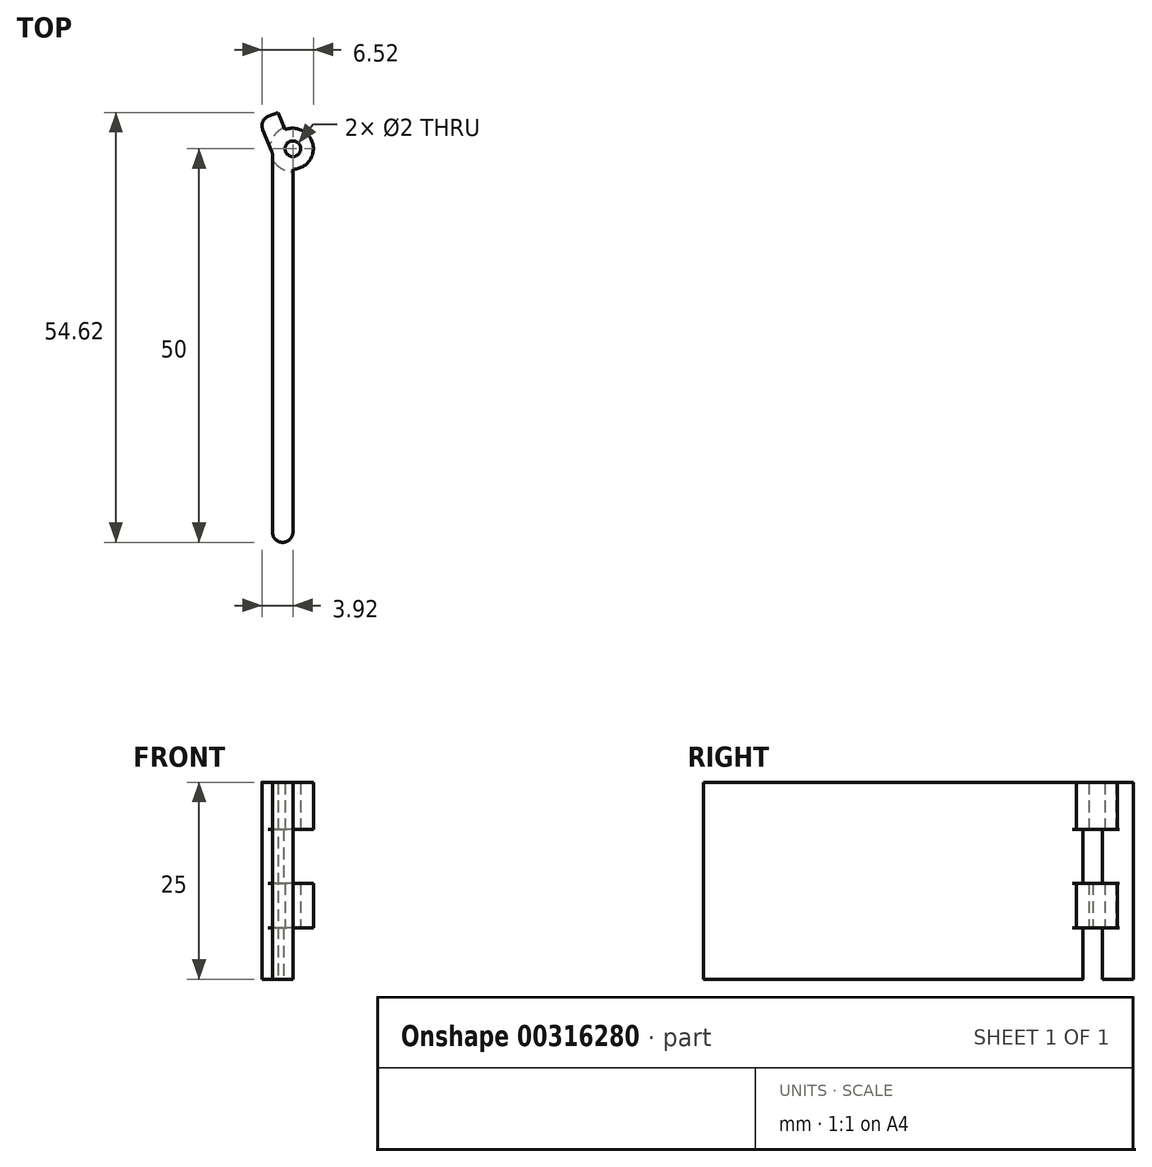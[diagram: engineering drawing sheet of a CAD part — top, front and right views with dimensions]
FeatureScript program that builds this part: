
annotation { "Feature Type Name" : "Feature", "Feature Type Description" : "" }
export const myFeature = defineFeature(function(context is Context, id is Id, definition is map)
    precondition{}
    {
        {
            var Q0;
            Q0=qCreatedBy(makeId("Top.planeOp"),FACE);
            var sketch = newSketch(context, id + "F0", { "sketchPlane" : qUnion([Q0])});
            skLineSegment(sketch, "E0", {"start": v(35.36, -35.36) * mm, "end": v(0, 0) * mm});
            skLineSegment(sketch, "E1", {"start": v(0, 0) * mm, "end": v(0, -50) * mm});
            skCircle(sketch, "E2", {"center": v(0, 0) * mm, "radius": 2.6 * mm});
            skLineSegment(sketch, "E3", {"start": v(0, 0) * mm, "end": v(-1.91, 4.62) * mm});
            skLineSegment(sketch, "E4", {"start": v(0, -50) * mm, "end": v(-2.6, -50) * mm});
            skLineSegment(sketch, "E5", {"start": v(-2.6, -50) * mm, "end": v(-2.6, 0) * mm});
            skCircle(sketch, "E6", {"center": v(0, 0) * mm, "radius": 1 * mm});
            skLineSegment(sketch, "E7", {"start": v(-1.91, 4.62) * mm, "end": v(-4.32, 3.62) * mm});
            skLineSegment(sketch, "E8", {"start": v(-4.32, 3.62) * mm, "end": v(-2.4, -1) * mm});
            skLineSegment(sketch, "E9", {"start": v(-1.91, 4.62) * mm, "end": v(0.49, 5.61) * mm});
            skLineSegment(sketch, "E10", {"start": v(0.49, 5.61) * mm, "end": v(2.4, 1) * mm});
            skLineSegment(sketch, "E11", {"start": v(35.36, -35.36) * mm, "end": v(37.2, -33.52) * mm});
            skLineSegment(sketch, "E12", {"start": v(37.2, -33.52) * mm, "end": v(1.84, 1.84) * mm});
            skSolve(sketch);
        }
        {
            var Q0;
            {var subQ0=sQuery(id+"F0.wireOp",EDGE,"E7");Q0=makeQuery(id+"F0.imprint","IMPRINT",FACE,{"disambiguationData":[TD([[makeQuery(id+"F0.imprint","IMPRINT",EDGE,{"derivedFrom":subQ0}),1.0]])]});}
            var Q1;
            {var subQ0=sQuery(id+"F0.wireOp",EDGE,"E5");var subQ1=sQuery(id+"F0.wireOp",EDGE,"E2");var subQ2=makeQuery(id+"F0.imprint","INTERSECT",VERTEX,{"derivedFrom":[subQ1,subQ0]});Q1=makeQuery(id+"F0.imprint","IMPRINT",FACE,{"disambiguationData":[TD([[makeQuery(id+"F0.imprint","IMPRINT",EDGE,{"disambiguationData":[TD([[subQ2,-1.0]])],"derivedFrom":subQ1}),-1.0]])]});}
            var Q2;
            {var subQ0=sQuery(id+"F0.wireOp",EDGE,"E2");var subQ2=sQuery(id+"F0.wireOp",EDGE,"E1");var subQ3=makeQuery(id+"F0.imprint","INTERSECT",VERTEX,{"derivedFrom":[subQ2,subQ0]});Q2=makeQuery(id+"F0.imprint","IMPRINT",FACE,{"disambiguationData":[TD([[makeQuery(id+"F0.imprint","IMPRINT",EDGE,{"disambiguationData":[TD([[subQ3,1.0]])],"derivedFrom":subQ2}),-1.0]])]});}
            var Q3;
            {var subQ1=sQuery(id+"F0.wireOp",EDGE,"E4");Q3=makeQuery(id+"F0.imprint","IMPRINT",FACE,{"disambiguationData":[TD([[makeQuery(id+"F0.imprint","IMPRINT",EDGE,{"derivedFrom":subQ1}),-1.0]])]});}
            var Q4;
            {var subQ0=sQuery(id+"F0.wireOp",EDGE,"E2");var subQ2=sQuery(id+"F0.wireOp",EDGE,"E0");var subQ3=makeQuery(id+"F0.imprint","INTERSECT",VERTEX,{"derivedFrom":[subQ2,subQ0]});Q4=makeQuery(id+"F0.imprint","IMPRINT",FACE,{"disambiguationData":[TD([[makeQuery(id+"F0.imprint","IMPRINT",EDGE,{"disambiguationData":[TD([[subQ3,-1.0]])],"derivedFrom":subQ2}),-1.0]])]});}
            var Q5;
            {var subQ0=sQuery(id+"F0.wireOp",EDGE,"E2");var subQ1=sQuery(id+"F0.wireOp",EDGE,"E0");var subQ2=makeQuery(id+"F0.imprint","INTERSECT",VERTEX,{"derivedFrom":[subQ1,subQ0]});Q5=makeQuery(id+"F0.imprint","IMPRINT",FACE,{"disambiguationData":[TD([[makeQuery(id+"F0.imprint","IMPRINT",EDGE,{"disambiguationData":[TD([[subQ2,-1.0]])],"derivedFrom":subQ1}),1.0]])]});}
            extrude(context, id + "F1", {"entities" : qUnion([Q0, Q1, Q2, Q3, Q4, Q5]), "depth" : 25 * mm});
        }
        {
            var Q0;
            Q0=makeQuery(id+"F1.opExtrude","CAP_FACE",FACE,{"disambiguationData":[OSD([sQuery(id+"F0.wireOp",EDGE,"E1"),sQuery(id+"F0.wireOp",EDGE,"E2"),sQuery(id+"F0.wireOp",EDGE,"E3"),sQuery(id+"F0.wireOp",EDGE,"E4"),sQuery(id+"F0.wireOp",EDGE,"E5"),sQuery(id+"F0.wireOp",EDGE,"E6"),sQuery(id+"F0.wireOp",EDGE,"E7"),sQuery(id+"F0.wireOp",EDGE,"E8")])],"isStart":false});
            var Q1;
            Q1=makeQuery(id+"F1.opExtrude","CAP_FACE",FACE,{"disambiguationData":[OSD([sQuery(id+"F0.wireOp",EDGE,"E1"),sQuery(id+"F0.wireOp",EDGE,"E2"),sQuery(id+"F0.wireOp",EDGE,"E3"),sQuery(id+"F0.wireOp",EDGE,"E4"),sQuery(id+"F0.wireOp",EDGE,"E5"),sQuery(id+"F0.wireOp",EDGE,"E6"),sQuery(id+"F0.wireOp",EDGE,"E7"),sQuery(id+"F0.wireOp",EDGE,"E8")])],"isStart":true});
            cPlane(context, id + "F2", {"entities" : qUnion([Q0, Q1]), "cplaneType" : CPlaneType.MID_PLANE, "offset" : 25 * mm, "width" : 150 * mm, "height" : 150 * mm});
        }
        {
            var Q0;
            Q0=qCreatedBy(id+"F2.planeOp",FACE);
            var Q1;
            Q1=makeQuery(id+"F1.opExtrude","CAP_FACE",FACE,{"disambiguationData":[OSD([sQuery(id+"F0.wireOp",EDGE,"E1"),sQuery(id+"F0.wireOp",EDGE,"E2"),sQuery(id+"F0.wireOp",EDGE,"E3"),sQuery(id+"F0.wireOp",EDGE,"E4"),sQuery(id+"F0.wireOp",EDGE,"E5"),sQuery(id+"F0.wireOp",EDGE,"E6"),sQuery(id+"F0.wireOp",EDGE,"E7"),sQuery(id+"F0.wireOp",EDGE,"E8")])],"isStart":true});
            cPlane(context, id + "F3", {"entities" : qUnion([Q0, Q1]), "cplaneType" : CPlaneType.MID_PLANE, "offset" : 25 * mm, "width" : 150 * mm, "height" : 150 * mm});
        }
        {
            var Q0;
            Q0=makeQuery(id+"F1.opExtrude","CAP_FACE",FACE,{"disambiguationData":[OSD([sQuery(id+"F0.wireOp",EDGE,"E1"),sQuery(id+"F0.wireOp",EDGE,"E2"),sQuery(id+"F0.wireOp",EDGE,"E3"),sQuery(id+"F0.wireOp",EDGE,"E4"),sQuery(id+"F0.wireOp",EDGE,"E5"),sQuery(id+"F0.wireOp",EDGE,"E6"),sQuery(id+"F0.wireOp",EDGE,"E7"),sQuery(id+"F0.wireOp",EDGE,"E8")])],"isStart":false});
            var Q1;
            Q1=qCreatedBy(id+"F2.planeOp",FACE);
            cPlane(context, id + "F4", {"entities" : qUnion([Q0, Q1]), "cplaneType" : CPlaneType.MID_PLANE, "offset" : 25 * mm, "width" : 150 * mm, "height" : 150 * mm});
        }
        {
            var Q0;
            {var subQ0=sQuery(id+"F0.wireOp",EDGE,"E2");var subQ2=sQuery(id+"F0.wireOp",EDGE,"E1");var subQ3=makeQuery(id+"F0.imprint","INTERSECT",VERTEX,{"derivedFrom":[subQ2,subQ0]});Q0=makeQuery(id+"F0.imprint","IMPRINT",FACE,{"disambiguationData":[TD([[makeQuery(id+"F0.imprint","IMPRINT",EDGE,{"disambiguationData":[TD([[subQ3,1.0]])],"derivedFrom":subQ2}),-1.0]])]});}
            var Q1;
            {var subQ0=sQuery(id+"F0.wireOp",EDGE,"E2");var subQ2=sQuery(id+"F0.wireOp",EDGE,"E0");var subQ3=makeQuery(id+"F0.imprint","INTERSECT",VERTEX,{"derivedFrom":[subQ2,subQ0]});Q1=makeQuery(id+"F0.imprint","IMPRINT",FACE,{"disambiguationData":[TD([[makeQuery(id+"F0.imprint","IMPRINT",EDGE,{"disambiguationData":[TD([[subQ3,-1.0]])],"derivedFrom":subQ2}),-1.0]])]});}
            var Q2;
            {var subQ0=sQuery(id+"F0.wireOp",EDGE,"E2");var subQ1=sQuery(id+"F0.wireOp",EDGE,"E0");var subQ2=makeQuery(id+"F0.imprint","INTERSECT",VERTEX,{"derivedFrom":[subQ1,subQ0]});Q2=makeQuery(id+"F0.imprint","IMPRINT",FACE,{"disambiguationData":[TD([[makeQuery(id+"F0.imprint","IMPRINT",EDGE,{"disambiguationData":[TD([[subQ2,-1.0]])],"derivedFrom":subQ1}),1.0]])]});}
            var Q3;
            Q3=qCreatedBy(id+"F3.planeOp",FACE);
            extrude(context, id + "F5", {"entities" : qUnion([Q0, Q1, Q2]), "endBound" : BoundingType.UP_TO_SURFACE, "endBoundEntityFace" : qUnion([Q3]), "depth" : 25 * mm});
        }
        {
            var Q0;
            {var subQ0=sQuery(id+"F0.wireOp",EDGE,"E2");var subQ2=sQuery(id+"F0.wireOp",EDGE,"E1");var subQ3=makeQuery(id+"F0.imprint","INTERSECT",VERTEX,{"derivedFrom":[subQ2,subQ0]});Q0=makeQuery(id+"F0.imprint","IMPRINT",FACE,{"disambiguationData":[TD([[makeQuery(id+"F0.imprint","IMPRINT",EDGE,{"disambiguationData":[TD([[subQ3,1.0]])],"derivedFrom":subQ2}),-1.0]])]});}
            var Q1;
            {var subQ0=sQuery(id+"F0.wireOp",EDGE,"E2");var subQ1=sQuery(id+"F0.wireOp",EDGE,"E0");var subQ2=makeQuery(id+"F0.imprint","INTERSECT",VERTEX,{"derivedFrom":[subQ1,subQ0]});Q1=makeQuery(id+"F0.imprint","IMPRINT",FACE,{"disambiguationData":[TD([[makeQuery(id+"F0.imprint","IMPRINT",EDGE,{"disambiguationData":[TD([[subQ2,-1.0]])],"derivedFrom":subQ1}),1.0]])]});}
            var Q2;
            {var subQ0=sQuery(id+"F0.wireOp",EDGE,"E2");var subQ2=sQuery(id+"F0.wireOp",EDGE,"E0");var subQ3=makeQuery(id+"F0.imprint","INTERSECT",VERTEX,{"derivedFrom":[subQ2,subQ0]});Q2=makeQuery(id+"F0.imprint","IMPRINT",FACE,{"disambiguationData":[TD([[makeQuery(id+"F0.imprint","IMPRINT",EDGE,{"disambiguationData":[TD([[subQ3,-1.0]])],"derivedFrom":subQ2}),-1.0]])]});}
            var Q3;
            Q3=qCreatedBy(id+"F4.planeOp",FACE);
            var Q4;
            Q4=qCreatedBy(id+"F2.planeOp",FACE);
            extrude(context, id + "F6", {"entities" : qUnion([Q0, Q1, Q2]), "endBound" : BoundingType.UP_TO_SURFACE, "endBoundEntityFace" : qUnion([Q3]), "depth" : 25 * mm, "hasSecondDirection" : true, "secondDirectionBound" : SecondDirectionBoundingType.UP_TO_SURFACE, "secondDirectionOppositeDirection" : false, "secondDirectionBoundEntityFace" : qUnion([Q4]), "secondDirectionDepth" : 25 * mm});
        }
        {
            var Q0;
            Q0=makeQuery(id+"F6.opExtrude","SWEPT_BODY",BODY,{"disambiguationData":[OSD([sQuery(id+"F0.wireOp",EDGE,"E2"),sQuery(id+"F0.wireOp",EDGE,"E6")])]});
            var Q1;
            Q1=makeQuery(id+"F5.opExtrude","SWEPT_BODY",BODY,{"disambiguationData":[OSD([sQuery(id+"F0.wireOp",EDGE,"E2"),sQuery(id+"F0.wireOp",EDGE,"E6")])]});
            var Q2;
            Q2=makeQuery(id+"F1.opExtrude","SWEPT_BODY",BODY,{"disambiguationData":[OSD([sQuery(id+"F0.wireOp",EDGE,"E1"),sQuery(id+"F0.wireOp",EDGE,"E2"),sQuery(id+"F0.wireOp",EDGE,"E3"),sQuery(id+"F0.wireOp",EDGE,"E4"),sQuery(id+"F0.wireOp",EDGE,"E5"),sQuery(id+"F0.wireOp",EDGE,"E6"),sQuery(id+"F0.wireOp",EDGE,"E7"),sQuery(id+"F0.wireOp",EDGE,"E8")])]});
            booleanBodies(context, id + "F7", {"operationType" : BooleanOperationType.SUBTRACTION, "tools" : qUnion([Q0, Q1]), "targets" : qUnion([Q2]), "offset" : true, "offsetAll" : true, "offsetDistance" : 0.3 * mm});
        }
        {
            var Q0;
            Q0=makeQuery(id+"F7.tempBoolean.opBoolean","INTERSECT",EDGE,{"derivedFrom":[makeQuery(id+"F1.opExtrude","SWEPT_FACE",FACE,{"disambiguationData":[OSD([sQuery(id+"F0.wireOp",EDGE,"E8")])]}),makeQuery(id+"F7.offsetTempBody.opPattern","COPY",FACE,{"derivedFrom":makeQuery(id+"F5.opExtrude","SWEPT_FACE",FACE,{"disambiguationData":[OSD([sQuery(id+"F0.wireOp",EDGE,"E2")])]}),"instanceName":"1"})]});
            var Q1;
            Q1=makeQuery(id+"F7.tempBoolean.opBoolean","INTERSECT",EDGE,{"derivedFrom":[makeQuery(id+"F1.opExtrude","SWEPT_FACE",FACE,{"disambiguationData":[OSD([sQuery(id+"F0.wireOp",EDGE,"E5")])]}),makeQuery(id+"F7.offsetTempBody.opPattern","COPY",FACE,{"derivedFrom":makeQuery(id+"F5.opExtrude","SWEPT_FACE",FACE,{"disambiguationData":[OSD([sQuery(id+"F0.wireOp",EDGE,"E2")])]}),"instanceName":"1"})]});
            var Q2;
            Q2=makeQuery(id+"F7.tempBoolean.opBoolean","INTERSECT",EDGE,{"derivedFrom":[makeQuery(id+"F1.opExtrude","SWEPT_FACE",FACE,{"disambiguationData":[OSD([sQuery(id+"F0.wireOp",EDGE,"E5")])]}),makeQuery(id+"F7.offsetTempBody.opPattern","COPY",FACE,{"derivedFrom":makeQuery(id+"F6.opExtrude","SWEPT_FACE",FACE,{"disambiguationData":[OSD([sQuery(id+"F0.wireOp",EDGE,"E2")])]}),"instanceName":"1"})]});
            var Q3;
            Q3=makeQuery(id+"F7.tempBoolean.opBoolean","INTERSECT",EDGE,{"derivedFrom":[makeQuery(id+"F1.opExtrude","SWEPT_FACE",FACE,{"disambiguationData":[OSD([sQuery(id+"F0.wireOp",EDGE,"E8")])]}),makeQuery(id+"F7.offsetTempBody.opPattern","COPY",FACE,{"derivedFrom":makeQuery(id+"F6.opExtrude","SWEPT_FACE",FACE,{"disambiguationData":[OSD([sQuery(id+"F0.wireOp",EDGE,"E2")])]}),"instanceName":"1"})]});
            var Q4;
            Q4=makeQuery(id+"F7.tempBoolean.opBoolean","INTERSECT",EDGE,{"derivedFrom":[makeQuery(id+"F1.opExtrude","SWEPT_FACE",FACE,{"disambiguationData":[OSD([sQuery(id+"F0.wireOp",EDGE,"E1")])]}),makeQuery(id+"F7.offsetTempBody.opPattern","COPY",FACE,{"derivedFrom":makeQuery(id+"F5.opExtrude","SWEPT_FACE",FACE,{"disambiguationData":[OSD([sQuery(id+"F0.wireOp",EDGE,"E2")])]}),"instanceName":"1"})]});
            var Q5;
            Q5=makeQuery(id+"F7.tempBoolean.opBoolean","INTERSECT",EDGE,{"derivedFrom":[makeQuery(id+"F1.opExtrude","SWEPT_FACE",FACE,{"disambiguationData":[OSD([sQuery(id+"F0.wireOp",EDGE,"E1")])]}),makeQuery(id+"F7.offsetTempBody.opPattern","COPY",FACE,{"derivedFrom":makeQuery(id+"F6.opExtrude","SWEPT_FACE",FACE,{"disambiguationData":[OSD([sQuery(id+"F0.wireOp",EDGE,"E2")])]}),"instanceName":"1"})]});
            var Q6;
            Q6=makeQuery(id+"F7.tempBoolean.opBoolean","INTERSECT",EDGE,{"derivedFrom":[makeQuery(id+"F1.opExtrude","SWEPT_FACE",FACE,{"disambiguationData":[OSD([sQuery(id+"F0.wireOp",EDGE,"E3")])]}),makeQuery(id+"F7.offsetTempBody.opPattern","COPY",FACE,{"derivedFrom":makeQuery(id+"F6.opExtrude","SWEPT_FACE",FACE,{"disambiguationData":[OSD([sQuery(id+"F0.wireOp",EDGE,"E2")])]}),"instanceName":"1"})]});
            var Q7;
            Q7=makeQuery(id+"F7.tempBoolean.opBoolean","INTERSECT",EDGE,{"derivedFrom":[makeQuery(id+"F1.opExtrude","SWEPT_FACE",FACE,{"disambiguationData":[OSD([sQuery(id+"F0.wireOp",EDGE,"E3")])]}),makeQuery(id+"F7.offsetTempBody.opPattern","COPY",FACE,{"derivedFrom":makeQuery(id+"F5.opExtrude","SWEPT_FACE",FACE,{"disambiguationData":[OSD([sQuery(id+"F0.wireOp",EDGE,"E2")])]}),"instanceName":"1"})]});
            fillet(context, id + "F8", {"entities" : qUnion([Q0, Q1, Q2, Q3, Q4, Q5, Q6, Q7]), "radius" : 0.2 * mm, "tangentPropagation" : true, "allowEdgeOverflow" : false});
        }
        {
            var Q0;
            Q0=makeQuery(id+"F1.opExtrude","SWEPT_EDGE",EDGE,{"disambiguationData":[OSD([sQuery(id+"F0.wireOp",EDGE,"E7"),sQuery(id+"F0.wireOp",EDGE,"E8")])]});
            var Q1;
            Q1=makeQuery(id+"F1.opExtrude","SWEPT_EDGE",EDGE,{"disambiguationData":[OSD([sQuery(id+"F0.wireOp",EDGE,"E1"),sQuery(id+"F0.wireOp",EDGE,"E4")])]});
            var Q2;
            Q2=makeQuery(id+"F1.opExtrude","SWEPT_EDGE",EDGE,{"disambiguationData":[OSD([sQuery(id+"F0.wireOp",EDGE,"E4"),sQuery(id+"F0.wireOp",EDGE,"E5")])]});
            var Q3;
            {var subQ0=sQuery(id+"F0.wireOp",EDGE,"E5");var subQ1=sQuery(id+"F0.wireOp",EDGE,"E8");Q3=makeQuery(id+"F7.tempBoolean.opBoolean","SPLIT",EDGE,{"disambiguationData":[TD([makeQuery(id+"F7.offsetTempBody.opPattern","COPY",FACE,{"derivedFrom":makeQuery(id+"F5.opExtrude","CAP_FACE",FACE,{"disambiguationData":[OSD([dummyQuery(id+"F3.planeOp",FACE)])],"isStart":false}),"instanceName":"1"})])],"derivedFrom":makeQuery(id+"F1.opExtrude","SWEPT_EDGE",EDGE,{"disambiguationData":[OSD([subQ0,subQ1])]})});}
            var Q4;
            {var subQ0=sQuery(id+"F0.wireOp",EDGE,"E8");var subQ1=sQuery(id+"F0.wireOp",EDGE,"E5");Q4=makeQuery(id+"F7.tempBoolean.opBoolean","SPLIT",EDGE,{"disambiguationData":[TD([makeQuery(id+"F1.opExtrude","CAP_FACE",FACE,{"disambiguationData":[OSD([sQuery(id+"F0.wireOp",EDGE,"E1"),sQuery(id+"F0.wireOp",EDGE,"E2"),sQuery(id+"F0.wireOp",EDGE,"E3"),sQuery(id+"F0.wireOp",EDGE,"E4"),subQ1,sQuery(id+"F0.wireOp",EDGE,"E6"),sQuery(id+"F0.wireOp",EDGE,"E7"),subQ0])],"isStart":false})])],"derivedFrom":makeQuery(id+"F1.opExtrude","SWEPT_EDGE",EDGE,{"disambiguationData":[OSD([subQ1,subQ0])]})});}
            fillet(context, id + "F9", {"entities" : qUnion([Q0, Q1, Q2, Q3, Q4]), "radius" : (2.6 / 2) * mm, "tangentPropagation" : true, "allowEdgeOverflow" : false});
        }
    });
